# Revit family: Line
name_source: partatom
category: Mechanical Equipment
units: mm (PartAtom-declared; Revit-internal decimal feet)

## family parameters
Always vertical = Yes
Classification = None
Cut with Voids When Loaded = No
Part Type = Normal
Room Calculation Point = No
Round Connector Dimension = Use Diameter
Shared = No
Work Plane-Based = No

## types (4) — shared parameters
00_20_Manufacturer = Blauberg
00_20_Name = Axial fan
Amperage = 0 A
Casing Material = Plastic, opaque, white
Description = For round channels
Frequency = 50 Hz
Grid Material = Mesh, kapron
Load Classification = HVAC
Maintenance zone material = <By Category>
Manufacturer = Blauberg
Number of Fase = 1
URL = https://blaubergventilatoren.de
Voltage = 230 V
e = 13 mm  [stored 0.0426509 ft]
zero-valued in all types: Default Elevation

## per-type parameters (varying)
| type | Apparent Load | Diameter | Dy | H | Height | L2 | Length | Maximum Air Flow | Power | Sound pressure level at 3 m distance | Weight | Width | a | c | d |
| Line 150 | 30 W | 150 mm | 145 mm  [stored 0.475722 ft] | 205 mm  [stored 0.672572 ft] | 205 mm  [stored 0.672572 ft] | 132 mm | 145 mm  [stored 0.475722 ft] | 292.0 m³/h | 24 W | 38 dBA | 0.92 kg | 205 mm  [stored 0.672572 ft] | 205 mm  [stored 0.672572 ft] | 132 mm | 150 mm |
| Line 100 | 21 W | 100 mm  [stored 0.328084 ft] | 95 mm  [stored 0.31168 ft] | 150 mm | 150 mm | 109 mm  [stored 0.357612 ft] | 122 mm | 95.0 m³/h | 14 W | 34 dBA | 0.58 kg | 150 mm | 150 mm | 109 mm  [stored 0.357612 ft] | 100 mm  [stored 0.328084 ft] |
| Line 125 | 23 W | 125 mm | 120 mm  [stored 0.393701 ft] | 176 mm | 176 mm | 114 mm | 127 mm | 180.0 m³/h | 16 W | 35 dBA | 0.74 kg | 176 mm | 176 mm | 114 mm | 125 mm |
| Line 120 | 23 W | 117 mm | 112 mm | 176 mm | 176 mm | 109 mm  [stored 0.357612 ft] | 122 mm | 174.0 m³/h | 17 W | 36 dBA | 0.74 kg | 176 mm | 176 mm | 109 mm  [stored 0.357612 ft] | 117 mm |

note: column(s) folded — value = type name in every type: 00_20_Type

note: [stored X ft] marks values corroborated as IEEE doubles in the binary element streams (Revit-internal decimal feet)
